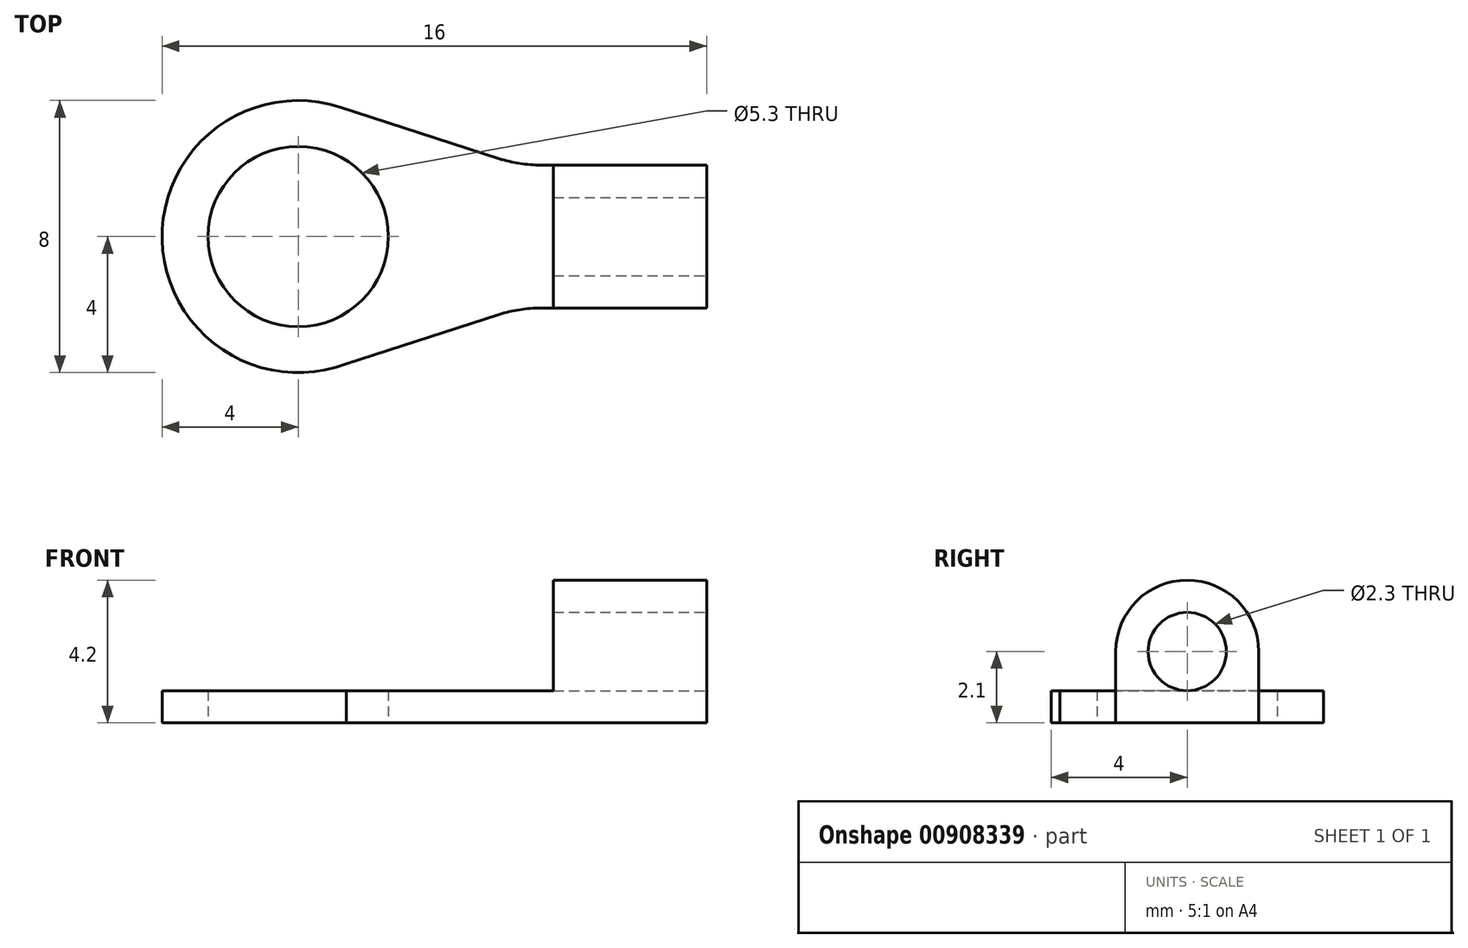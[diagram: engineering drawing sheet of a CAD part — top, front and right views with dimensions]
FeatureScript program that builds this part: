
annotation { "Feature Type Name" : "Feature", "Feature Type Description" : "" }
export const myFeature = defineFeature(function(context is Context, id is Id, definition is map)
    precondition{}
    {
        {
            var Q0;
            Q0=qCreatedBy(makeId("Top.planeOp"),FACE);
            var sketch = newSketch(context, id + "F0", { "sketchPlane" : qUnion([Q0])});
            skLineSegment(sketch, "E0.left", {"start": v(0, 4) * mm, "end": v(0, 4) * mm});
            skLineSegment(sketch, "E0.right", {"start": v(16, 1.9) * mm, "end": v(16, 6.1) * mm});
            skPoint(sketch, "E1.visualSharp", {"position": v(0, 8) * mm});
            skArc(sketch, "E1.filletArc", {"start": v(4, 8) * mm, "mid": v(1.17, 6.83) * mm, "end": v(0, 4) * mm});
            skPoint(sketch, "E2.visualSharp", {"position": v(0, 0) * mm});
            skArc(sketch, "E2.filletArc", {"start": v(0, 4) * mm, "mid": v(1.17, 1.17) * mm, "end": v(4, 0) * mm});
            skLineSegment(sketch, "E3.bottom", {"start": v(16, 1.9) * mm, "end": v(11.13, 1.9) * mm});
            skLineSegment(sketch, "E3.top", {"start": v(16, 6.1) * mm, "end": v(11.13, 6.1) * mm});
            skPoint(sketch, "E3.middle", {"position": v(16, 4) * mm});
            skArc(sketch, "E4", {"start": v(5.23, 7.8) * mm, "mid": v(0, 3.9) * mm, "end": v(5.42, 0.26) * mm});
            skCircle(sketch, "E5", {"center": v(4, 4) * mm, "radius": 2.65 * mm});
            skLineSegment(sketch, "E6", {"start": v(9.9, 6.3) * mm, "end": v(5.23, 7.8) * mm});
            skLineSegment(sketch, "E7", {"start": v(9.9, 1.7) * mm, "end": v(5.42, 0.26) * mm});
            skPoint(sketch, "E8.visualSharp", {"position": v(10.5, 6.1) * mm});
            skArc(sketch, "E8.filletArc", {"start": v(9.9, 6.3) * mm, "mid": v(10.5, 6.15) * mm, "end": v(11.13, 6.1) * mm});
            skPoint(sketch, "E9.visualSharp", {"position": v(10.5, 1.9) * mm});
            skArc(sketch, "E9.filletArc", {"start": v(11.13, 1.9) * mm, "mid": v(10.5, 1.85) * mm, "end": v(9.9, 1.7) * mm});
            skPoint(sketch, "E10.orphan", {"position": v(20.5, 6.1) * mm});
            skPoint(sketch, "E11.orphan", {"position": v(20.5, 1.9) * mm});
            skPoint(sketch, "E0.top.end.orphan", {"position": v(16, 8) * mm});
            skPoint(sketch, "E0.bottom.end.orphan", {"position": v(16, 0) * mm});
            skPoint(sketch, "E3.right.end.orphan", {"position": v(11.5, 6.1) * mm});
            skPoint(sketch, "E3.right.start.orphan", {"position": v(11.5, 1.9) * mm});
            skSolve(sketch);
        }
        {
            var Q0;
            Q0=makeQuery(id+"F0.imprint","IMPRINT",FACE,{"disambiguationData":[TD([[makeQuery(id+"F0.imprint","IMPRINT",EDGE,{"derivedFrom":sQuery(id+"F0.wireOp",EDGE,"E0.right")}),1.0]])]});
            extrude(context, id + "F1", {"entities" : qUnion([Q0]), "depth" : 0.95 * mm, "offsetDistance" : 25 * mm});
        }
        {
            var Q0;
            Q0=makeQuery(id+"F1.opExtrude","CAP_FACE",FACE,{"disambiguationData":[OSD([sQuery(id+"F0.wireOp",EDGE,"E0.right"),sQuery(id+"F0.wireOp",EDGE,"E3.bottom"),sQuery(id+"F0.wireOp",EDGE,"E3.top"),sQuery(id+"F0.wireOp",EDGE,"E4"),sQuery(id+"F0.wireOp",EDGE,"E5"),sQuery(id+"F0.wireOp",EDGE,"E6"),sQuery(id+"F0.wireOp",EDGE,"E7"),sQuery(id+"F0.wireOp",EDGE,"E8.filletArc"),sQuery(id+"F0.wireOp",EDGE,"E9.filletArc")])],"isStart":false});
            var sketch = newSketch(context, id + "F2", { "sketchPlane" : qUnion([Q0])});
            skLineSegment(sketch, "E12.bottom", {"start": v(16, 6.1) * mm, "end": v(11.5, 6.1) * mm});
            skLineSegment(sketch, "E12.top", {"start": v(16, 1.9) * mm, "end": v(11.5, 1.9) * mm});
            skLineSegment(sketch, "E12.left", {"start": v(16, 6.1) * mm, "end": v(16, 1.9) * mm});
            skLineSegment(sketch, "E12.right", {"start": v(11.5, 6.1) * mm, "end": v(11.5, 1.9) * mm});
            skSolve(sketch);
        }
        {
            var Q0;
            Q0 = qSketchRegion(id + "F2", true);
            extrude(context, id + "F3", {"entities" : qUnion([Q0]), "operationType" : NewBodyOperationType.ADD, "depth" : 3.25 * mm, "offsetDistance" : 25 * mm});
        }
        {
            var Q0;
            Q0=makeQuery(id+"F3.opExtrude","CAP_EDGE",EDGE,{"disambiguationData":[OSD([sQuery(id+"F2.wireOp",EDGE,"E12.bottom")])],"isStart":false});
            var Q1;
            Q1=makeQuery(id+"F3.opExtrude","CAP_EDGE",EDGE,{"disambiguationData":[OSD([sQuery(id+"F2.wireOp",EDGE,"E12.top")])],"isStart":false});
            fillet(context, id + "F4", {"entities" : qUnion([Q0, Q1]), "radius" : 2.1 * mm, "tangentPropagation" : true, "allowEdgeOverflow" : false});
        }
        {
            var Q0;
            Q0=makeQuery(id+"F3.boolean.opBoolean","MERGE",FACE,{"derivedFrom":[makeQuery(id+"F1.opExtrude","SWEPT_FACE",FACE,{"disambiguationData":[OSD([sQuery(id+"F0.wireOp",EDGE,"E0.right")])]}),makeQuery(id+"F3.opExtrude","SWEPT_FACE",FACE,{"disambiguationData":[OSD([sQuery(id+"F2.wireOp",EDGE,"E12.left")])]})]});
            var sketch = newSketch(context, id + "F5", { "sketchPlane" : qUnion([Q0])});
            skCircle(sketch, "E13", {"center": v(4, 2.1) * mm, "radius": 1.15 * mm});
            skSolve(sketch);
        }
        {
            var Q0;
            Q0=makeQuery(id+"F5.imprint","IMPRINT",FACE,{"disambiguationData":[TD([[makeQuery(id+"F5.imprint","IMPRINT",EDGE,{"derivedFrom":sQuery(id+"F5.wireOp",EDGE,"E13")}),1.0]])]});
            extrude(context, id + "F6", {"entities" : qUnion([Q0]), "operationType" : NewBodyOperationType.REMOVE, "oppositeDirection" : true, "depth" : 25 * mm, "offsetDistance" : 25 * mm});
        }
    });
